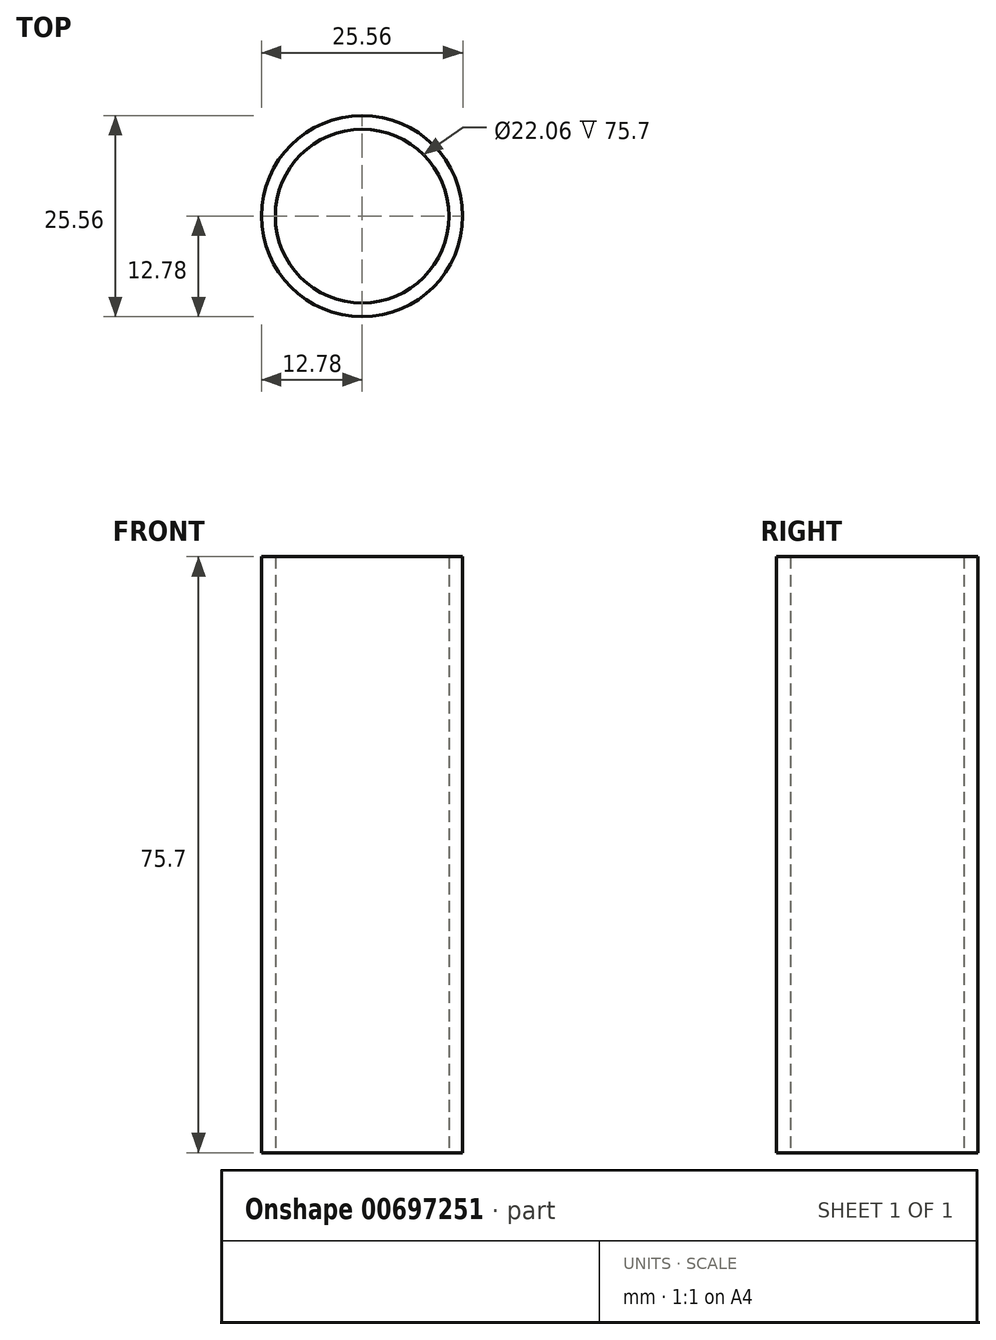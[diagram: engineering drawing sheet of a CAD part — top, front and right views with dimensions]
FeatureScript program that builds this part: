
annotation { "Feature Type Name" : "Feature", "Feature Type Description" : "" }
export const myFeature = defineFeature(function(context is Context, id is Id, definition is map)
    precondition{}
    {
        {
            var Q0;
            Q0=qCreatedBy(makeId("Top.planeOp"),FACE);
            var sketch = newSketch(context, id + "F0", { "sketchPlane" : qUnion([Q0])});
            skCircle(sketch, "E0", {"center": v(0, 0) * mm, "radius": 11.03 * mm});
            skCircle(sketch, "E1", {"center": v(0, 0) * mm, "radius": 12.78 * mm});
            skSolve(sketch);
        }
        {
            var Q0;
            Q0=makeQuery(id+"F0.imprint","IMPRINT",FACE,{"disambiguationData":[TD([[makeQuery(id+"F0.imprint","IMPRINT",EDGE,{"derivedFrom":sQuery(id+"F0.wireOp",EDGE,"E0")}),-1.0]])]});
            var Q1;
            Q1=sQuery(id+"F0.wireOp",EDGE,"E1");
            extrude(context, id + "F1", {"entities" : qUnion([Q0]), "surfaceEntities" : qUnion([Q1]), "depth" : 75.7 * mm, "offsetDistance" : 25 * mm});
        }
    });
